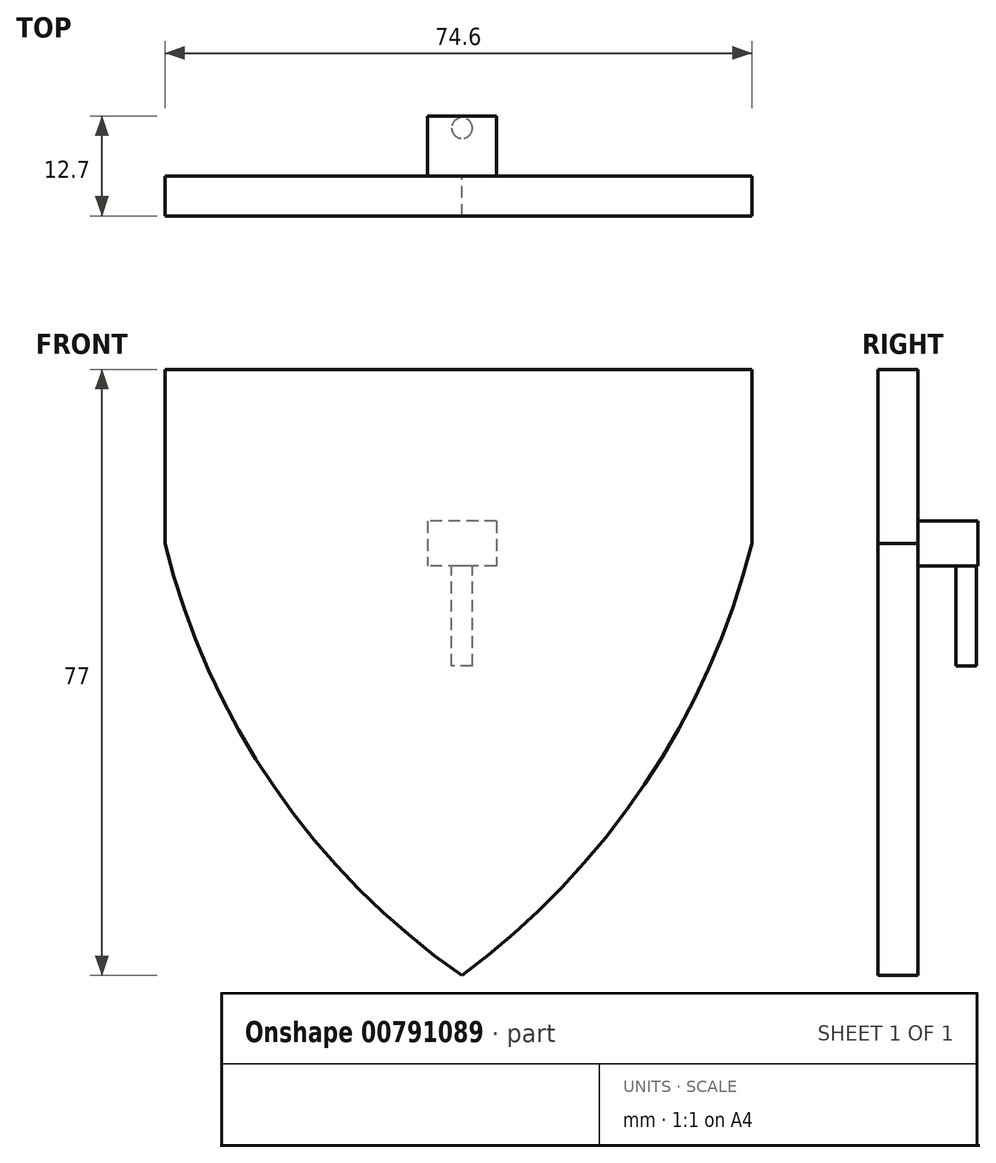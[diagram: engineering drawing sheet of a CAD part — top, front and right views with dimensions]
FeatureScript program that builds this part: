
annotation { "Feature Type Name" : "Feature", "Feature Type Description" : "" }
export const myFeature = defineFeature(function(context is Context, id is Id, definition is map)
    precondition{}
    {
        {
            var Q0;
            Q0=qCreatedBy(makeId("Front.planeOp"),FACE);
            var sketch = newSketch(context, id + "F0", { "sketchPlane" : qUnion([Q0])});
            skArc(sketch, "E0", {"start": v(0, -54.9) * mm, "mid": v(23.17, -30.63) * mm, "end": v(36.85, 0) * mm});
            skArc(sketch, "E1", {"start": v(-37.75, 0) * mm, "mid": v(-23.88, -30.9) * mm, "end": v(0, -54.9) * mm});
            skLineSegment(sketch, "E2", {"start": v(-37.75, 0) * mm, "end": v(-37.75, 21.2) * mm});
            skLineSegment(sketch, "E3", {"start": v(36.85, 0) * mm, "end": v(36.85, 22.1) * mm});
            skLineSegment(sketch, "E4", {"start": v(36.85, 22.1) * mm, "end": v(-37.75, 22.1) * mm});
            skLineSegment(sketch, "E5", {"start": v(-37.75, 22.1) * mm, "end": v(-37.75, 21.2) * mm});
            skSolve(sketch);
        }
        {
            var Q0;
            Q0 = qSketchRegion(id + "F0", true);
            extrude(context, id + "F1", {"entities" : qUnion([Q0]), "depth" : 5.08 * mm, "offsetDistance" : 25.4 * mm});
        }
        {
            var Q0;
            Q0=makeQuery(id+"F1.opExtrude","CAP_FACE",FACE,{"disambiguationData":[OSD([sQuery(id+"F0.wireOp",EDGE,"E0"),sQuery(id+"F0.wireOp",EDGE,"E1"),sQuery(id+"F0.wireOp",EDGE,"E2"),sQuery(id+"F0.wireOp",EDGE,"E3"),sQuery(id+"F0.wireOp",EDGE,"E4"),sQuery(id+"F0.wireOp",EDGE,"E5")])],"isStart":true});
            var sketch = newSketch(context, id + "F2", { "sketchPlane" : qUnion([Q0])});
            skLineSegment(sketch, "E6.bottom", {"start": v(-4.36, 2.86) * mm, "end": v(4.36, 2.86) * mm});
            skLineSegment(sketch, "E6.top", {"start": v(-4.36, -2.86) * mm, "end": v(4.36, -2.86) * mm});
            skLineSegment(sketch, "E6.left", {"start": v(-4.36, 2.86) * mm, "end": v(-4.36, -2.86) * mm});
            skLineSegment(sketch, "E6.right", {"start": v(4.36, 2.86) * mm, "end": v(4.36, -2.86) * mm});
            skPoint(sketch, "E6.middle", {"position": v(0, 0) * mm});
            skSolve(sketch);
        }
        {
            var Q0;
            Q0 = qSketchRegion(id + "F2", true);
            extrude(context, id + "F3", {"entities" : qUnion([Q0]), "operationType" : NewBodyOperationType.ADD, "depth" : 7.62 * mm, "offsetDistance" : 25.4 * mm});
        }
        {
            var Q0;
            Q0=makeQuery(id+"F3.opExtrude","SWEPT_FACE",FACE,{"disambiguationData":[OSD([sQuery(id+"F2.wireOp",EDGE,"E6.top")])]});
            var sketch = newSketch(context, id + "F4", { "sketchPlane" : qUnion([Q0])});
            skCircle(sketch, "E7", {"center": v(0, -6.09) * mm, "radius": 1.32 * mm});
            skSolve(sketch);
        }
        {
            var Q0;
            Q0 = qSketchRegion(id + "F4", true);
            extrude(context, id + "F5", {"entities" : qUnion([Q0]), "operationType" : NewBodyOperationType.ADD, "depth" : 12.7 * mm, "offsetDistance" : 25.4 * mm});
        }
    });
